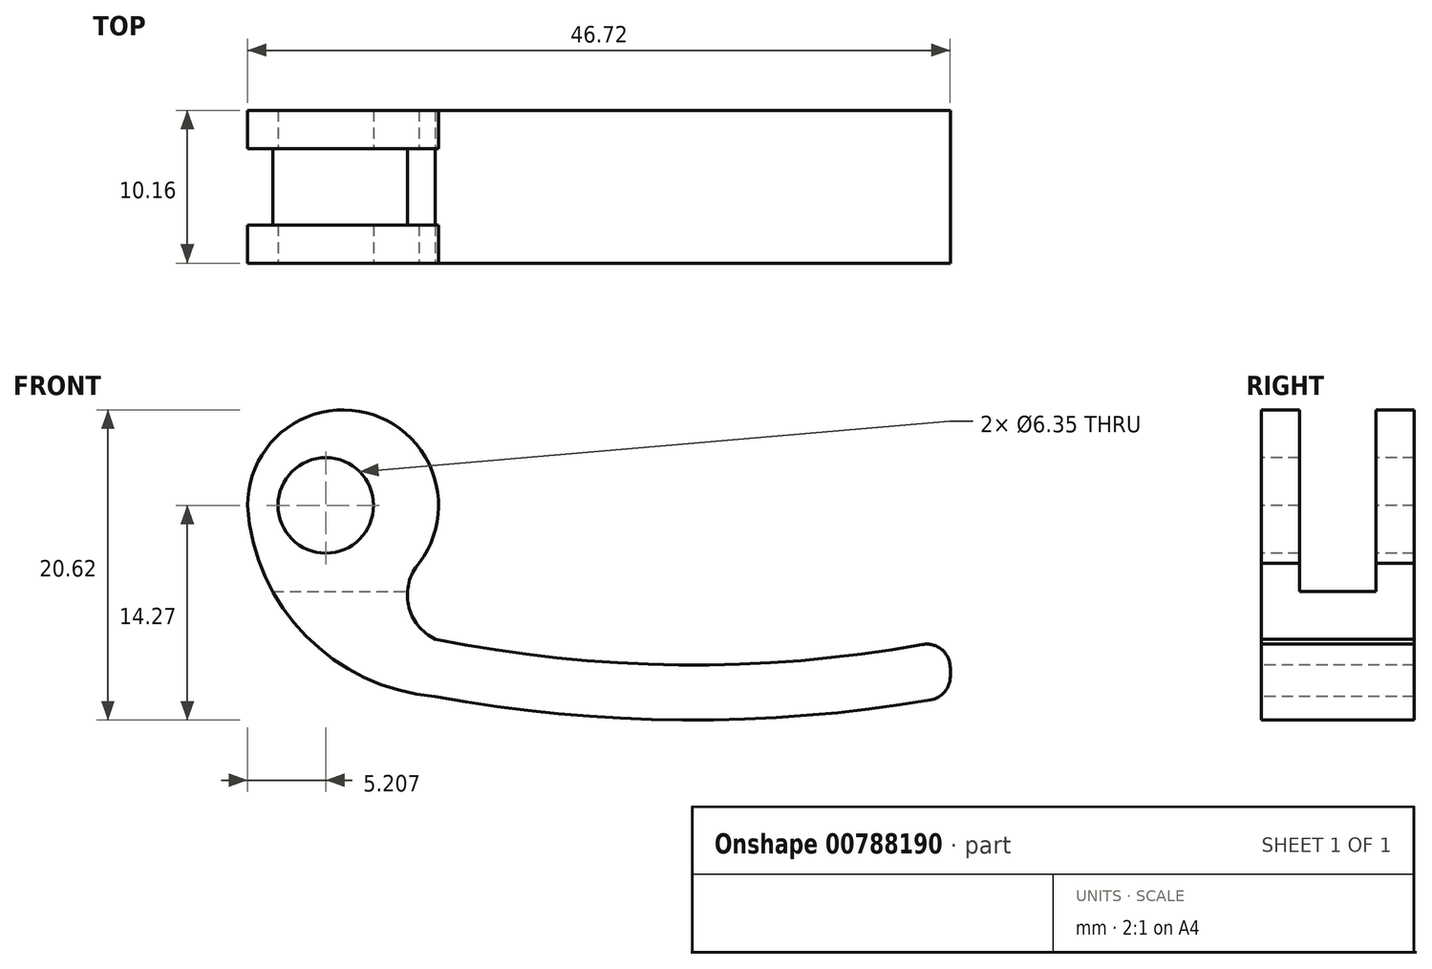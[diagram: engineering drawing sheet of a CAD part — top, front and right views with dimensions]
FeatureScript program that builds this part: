
annotation { "Feature Type Name" : "Feature", "Feature Type Description" : "" }
export const myFeature = defineFeature(function(context is Context, id is Id, definition is map)
    precondition{}
    {
        {
            var Q0;
            Q0=qCreatedBy(makeId("Front.planeOp"),FACE);
            var sketch = newSketch(context, id + "F0", { "sketchPlane" : qUnion([Q0])});
            skArc(sketch, "E0", {"start": v(5.06, -3.84) * mm, "mid": v(2.02, 6.02) * mm, "end": v(-6.35, 0) * mm});
            skCircle(sketch, "E1", {"center": v(-1.14, 0) * mm, "radius": 3.18 * mm});
            skPoint(sketch, "E2.end.orphan", {"position": v(-7.62, -17.78) * mm});
            skArc(sketch, "E3", {"start": v(6.13, -8.9) * mm, "mid": v(23.25, -10.61) * mm, "end": v(40.37, -8.9) * mm});
            skArc(sketch, "E4", {"start": v(6.13, -12.7) * mm, "mid": v(23.25, -14.27) * mm, "end": v(40.37, -12.7) * mm});
            skPoint(sketch, "E4.startSnap0", {"position": v(40.37, -12.7) * mm});
            skLineSegment(sketch, "E5", {"start": v(40.37, -8.89) * mm, "end": v(40.37, -12.7) * mm});
            skLineSegment(sketch, "E6", {"start": v(6.13, -8.89) * mm, "end": v(6.13, -12.7) * mm, "construction": true});
            skArc(sketch, "E7", {"start": v(-6.35, 0) * mm, "mid": v(-2.47, -8.67) * mm, "end": v(6.13, -12.7) * mm});
            skArc(sketch, "E8", {"start": v(5.06, -3.84) * mm, "mid": v(4.35, -6.63) * mm, "end": v(6.13, -8.9) * mm});
            skSolve(sketch);
        }
        {
            var Q0;
            Q0=qSketchRegion(id+"F0",true);
            extrude(context, id + "F1", {"entities" : qUnion([Q0]), "oppositeDirection" : true, "depth" : 10.16 * mm});
        }
        {
            var Q0;
            Q0=qCreatedBy(makeId("Right.planeOp"),FACE);
            var sketch = newSketch(context, id + "F2", { "sketchPlane" : qUnion([Q0])});
            skLineSegment(sketch, "E9.bottom", {"start": v(2.54, 7.62) * mm, "end": v(7.62, 7.62) * mm});
            skLineSegment(sketch, "E9.top", {"start": v(2.54, -5.72) * mm, "end": v(7.62, -5.72) * mm});
            skLineSegment(sketch, "E9.left", {"start": v(2.54, 7.62) * mm, "end": v(2.54, -5.72) * mm});
            skLineSegment(sketch, "E9.right", {"start": v(7.62, 7.62) * mm, "end": v(7.62, -5.72) * mm});
            skSolve(sketch);
        }
        {
            var Q0;
            Q0=qSketchRegion(id+"F2",true);
            extrude(context, id + "F3", {"entities" : qUnion([Q0]), "operationType" : NewBodyOperationType.REMOVE, "endBound" : BoundingType.SYMMETRIC, "oppositeDirection" : true, "depth" : 25.4 * mm});
        }
        {
            var Q0;
            Q0=makeQuery(id+"F1.opExtrude","SWEPT_EDGE",EDGE,{"disambiguationData":[OSD([sQuery(id+"F0.wireOp",EDGE,"E3"),sQuery(id+"F0.wireOp",EDGE,"E5")])]});
            var Q1;
            Q1=makeQuery(id+"F1.opExtrude","SWEPT_EDGE",EDGE,{"disambiguationData":[OSD([sQuery(id+"F0.wireOp",EDGE,"E4"),sQuery(id+"F0.wireOp",EDGE,"E5")])]});
            fillet(context, id + "F4", {"entities" : qUnion([Q0, Q1]), "radius" : 1.57 * mm, "tangentPropagation" : true, "allowEdgeOverflow" : false});
        }
    });
